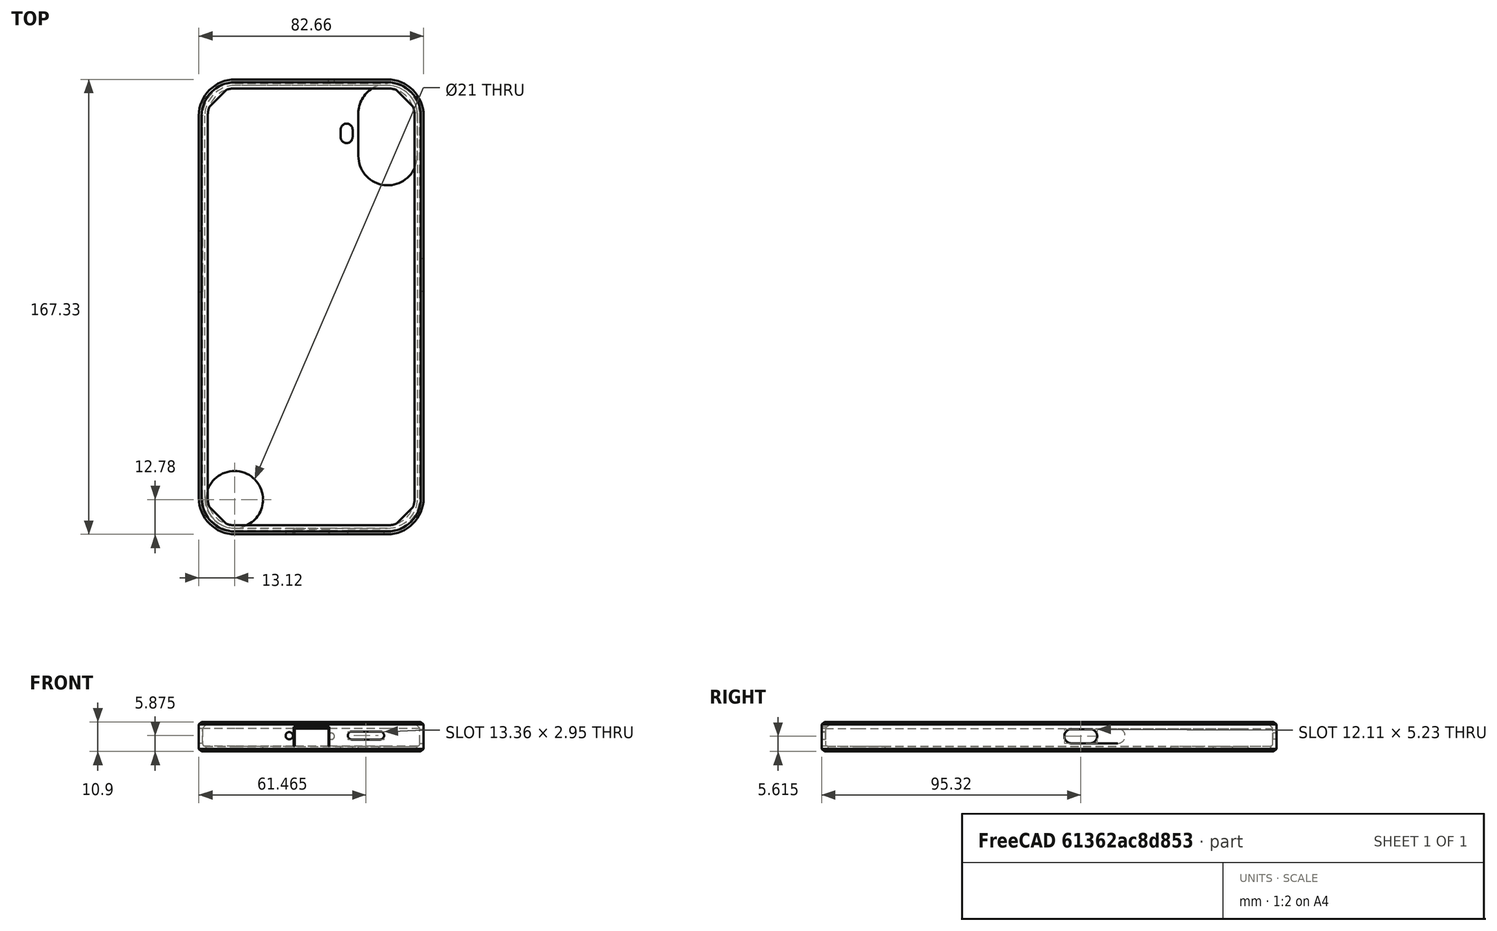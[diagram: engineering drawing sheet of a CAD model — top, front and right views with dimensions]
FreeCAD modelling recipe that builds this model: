
FCSTD DOCUMENT  (FreeCAD 0.22R38506 (Git))
Label: cmf_phone_1_v3
License: All rights reserved
LicenseURL: https://en.wikipedia.org/wiki/All_rights_reserved
objects: Sketcher::SketchObject×8, PartDesign::Pocket×4, Mesh::Feature×2, PartDesign::Pad×2, App::LinkGroup×1, PartDesign::AdditivePipe×1, PartDesign::Plane×1, PartDesign::Mirrored×1, PartDesign::Body×1, App::Part×1, Image::ImagePlane×1
note: 41 computed .brp shape members not serialized (recipe doc carries the construction recipe); baked Part::Feature solids carry a one-line shape summary decoded from their .brp

FEATURE [Mesh::Feature] cmf1_case  label="cmf1-case"
  Placement = pos=(-575.3,0,-7.05e-14) rot=(0,1,0;3.14159rad)
FEATURE [App::LinkGroup] LinkGroup
  ElementList = -> [cmf1_case]
  LinkMode = 0
  Placement = pos=(0.5,-5.96046e-08,0.4) rot=(0,0,1;0rad)
FEATURE [Sketcher::SketchObject] Sketch001  label="ProfilePathSketch"
  ArcFitTolerance = 1e-06
  AttachmentSupport = -> [XY_Plane001]
  FullyConstrained = false
  MakeInternals = false
  MapMode = 5
  sketch-geometry (5):
    g0: LineSegment StartX=0 StartY=-83.68 StartZ=0 EndX=28 EndY=-83.68 EndZ=0
    g1: ArcOfCircle CenterX=28 CenterY=-71.3528 CenterZ=0 NormalX=0 NormalY=0 NormalZ=1 AngleXU=0 Radius=12.3272 StartAngle=4.71239 EndAngle=6.28319
    g2: LineSegment StartX=40.3272 StartY=-71.3528 StartZ=0 EndX=40.3272 EndY=69.3228 EndZ=0
    g3: ArcOfCircle CenterX=28 CenterY=69.3228 CenterZ=0 NormalX=0 NormalY=0 NormalZ=1 AngleXU=0 Radius=12.3272 StartAngle=2e-16 EndAngle=1.5708
    g4: LineSegment StartX=28 StartY=81.65 StartZ=0 EndX=0 EndY=81.65 EndZ=0
  constraints (13):
    c: PointOnObject(g0,g-2)
    c: Horizontal(g0)
    c: Tangent(g1,g0) = -1.5708
    c: Vertical(g2)
    c: Tangent(g2,g1) = -1.5708
    c: DistanceX(g-1,g0) = 28
    c: DistanceY(g0,g-1) = 83.68
    c: PointOnObject(g4,g-2)
    c: Horizontal(g4)
    c: Equal(g0,g4)
    c: DistanceY(g0,g4) = 165.33
    c: Tangent(g4,g3) = -1.5708
    c: Tangent(g3,g2) = -1.5708
FEATURE [Sketcher::SketchObject] Sketch  label="ProfileSketch"
  ArcFitTolerance = 1e-06
  AttachmentSupport = -> [Sketch001]
  FullyConstrained = false
  MakeInternals = false
  MapMode = 7
  Placement = pos=(0,-83.68,0) rot=(0.57735,-0.57735,-0.57735;2.0944rad)
  sketch-geometry (11):
    g0: ArcOfCircle CenterX=-1.2 CenterY=2.8 CenterZ=0 NormalX=0 NormalY=0 NormalZ=1 AngleXU=0 Radius=0.8 StartAngle=4.71239 EndAngle=6.28319
    g1: LineSegment StartX=-0.4 StartY=2.8 StartZ=0 EndX=-0.4 EndY=8.4 EndZ=0
    g2: ArcOfCircle CenterX=-1.46903 CenterY=8.10997 CenterZ=0 NormalX=0 NormalY=0 NormalZ=1 AngleXU=0 Radius=1.10767 StartAngle=0.264929 EndAngle=0.855211
    g3: LineSegment StartX=-0.742328 StartY=8.94594 StartZ=0 EndX=-2.3 EndY=10.3 EndZ=0
    g4: LineSegment StartX=-2.3 StartY=10.3 StartZ=0 EndX=-2.3 EndY=10.9 EndZ=0
    g5: LineSegment StartX=-1.2 StartY=2 StartZ=0 EndX=-1.2 EndY=0 EndZ=0
    g6: LineSegment StartX=-1.2 StartY=0 StartZ=0 EndX=0 EndY=0 EndZ=0
    g7: LineSegment StartX=0 StartY=0 StartZ=0 EndX=1 EndY=1 EndZ=0
    g8: LineSegment StartX=1 StartY=1 StartZ=0 EndX=1 EndY=9.9 EndZ=0
    g9: LineSegment StartX=1 StartY=9.9 StartZ=0 EndX=-4e-16 EndY=10.9 EndZ=0
    g10: LineSegment StartX=-2.3 StartY=10.9 StartZ=0 EndX=-4e-16 EndY=10.9 EndZ=0
  constraints (31):
    c: Vertical(g1)
    c: Coincident(g2,g1)
    c: Angle(g3,g1) = 2.28638
    c: Coincident(g4,g3)
    c: Vertical(g4)
    c: Radius(g0) = 0.8
    c: Tangent(g1,g0) = -1.5708
    c: Coincident(g5,g0)
    c: Vertical(g5)
    c: Perpendicular(g0,g5)
    c: DistanceY(g5,g5) = 2  'bottom'
    c: Coincident(g6,g5)
    c: Horizontal(g6)
    c: DistanceX(g6,g6) = 1.2
    c: Coincident(g7,g6)
    c: Angle(g7,g6) = 2.35619
    c: DistanceY(g7,g7) = 1
    c: Coincident(g8,g7)
    c: Vertical(g8)
    c: Coincident(g8,g9)
    c: Angle(g9,g8) = 2.35619
    c: Coincident(g10,g4)
    c: Coincident(g10,g9)
    c: Horizontal(g10)
    c: Equal(g7,g9)
    c: Tangent(g3,g2) = -1.5708
    c: DistanceY(g1,g1) = 5.6
    c: Coincident(g6,g-1)
    c: Distance(g4,g4) = 0.6
    c: DistanceX(g3,g0) = 1.1
    c: DistanceY(g0,g3) = 8.3
FEATURE [PartDesign::AdditivePipe] AdditivePipe
  AuxilleryCurvelinear = true
  AuxillerySpineTangent = false
  Binormal = (0,0,0)
  Mode = 0
  Profile = -> Sketch
  Refine = true
  Spine = -> Sketch001 [Edge1,Edge2,Edge3,Edge4,Edge5]
  SpineTangent = false
  Suppressed = false
  Transformation = 0
  Transition = 0
FEATURE [PartDesign::Plane] DatumPlane  label="CaseTopDatumPlane"
  AttachmentSupport = -> [AdditivePipe]
  Length = 106.175
  MapMode = 5
  Placement = pos=(0,0,10.9) rot=(0,0,1;0rad)
  ResizeMode = 0
  Width = 190.851
FEATURE [Sketcher::SketchObject] Sketch002  label="CornerClampSketch"
  ArcFitTolerance = 1e-06
  AttachmentSupport = -> [DatumPlane]
  ExternalGeometry = -> [AdditivePipe]
  FullyConstrained = true
  MakeInternals = false
  MapMode = 5
  Placement = pos=(0,0,10.9) rot=(0,0,1;0rad)
  sketch-geometry (8):
    g0: LineSegment StartX=31.2599 StartY=-80.8353 StartZ=0 EndX=37.4825 EndY=-74.6127 EndZ=0
    g1: ArcOfCircle CenterX=28 CenterY=-71.3528 CenterZ=0 NormalX=0 NormalY=0 NormalZ=1 AngleXU=0 Radius=10.0272 StartAngle=5.04352 EndAngle=5.95206
    g2: LineSegment [constr] StartX=28 StartY=-81.38 StartZ=0 EndX=31.2599 EndY=-80.8353 EndZ=0
    g3: LineSegment [constr] StartX=38.0272 StartY=-71.3528 StartZ=0 EndX=37.4825 EndY=-74.6127 EndZ=0
    g4: LineSegment StartX=31.2599 StartY=78.8053 StartZ=0 EndX=37.4825 EndY=72.5827 EndZ=0
    g5: LineSegment [constr] StartX=28 StartY=79.35 StartZ=0 EndX=31.2599 EndY=78.8053 EndZ=0
    g6: LineSegment [constr] StartX=38.0272 StartY=69.3228 StartZ=0 EndX=37.4825 EndY=72.5827 EndZ=0
    g7: ArcOfCircle CenterX=28 CenterY=69.3228 CenterZ=0 NormalX=0 NormalY=0 NormalZ=1 AngleXU=0 Radius=10.0272 StartAngle=0.331128 EndAngle=1.23967
  constraints (21):
    c: PointOnObject(g0,g-3)
    c: Tangent(g1,g-3) = -1.5708
    c: Coincident(g0,g1)
    c: Coincident(g0,g1)
    c: Coincident(g2,g-3)
    c: Coincident(g3,g0)
    c: Coincident(g0,g2)
    c: Equal(g3,g2)
    c: Distance(g0,g0) = 8.8
    c: PointOnObject(g4,g-4)
    c: PointOnObject(g4,g-4)
    c: Coincident(g5,g-4)
    c: Coincident(g5,g4)
    c: Coincident(g6,g-4)
    c: Coincident(g6,g4)
    c: Equal(g6,g5)
    c: Coincident(g7,g4)
    c: Coincident(g7,g4)
    c: Equal(g-4,g7)
    c: Equal(g4,g0)
    c: Coincident(g3,g-3)
FEATURE [PartDesign::Pad] Pad  label="CornerClampPad"
  BaseFeature = -> AdditivePipe
  Direction = (0,0,1)
  Length = 0.6
  Length2 = 10
  Profile = -> Sketch002
  ReferenceAxis = -> Sketch002 [N_Axis]
  Refine = true
  Reversed = true
  Suppressed = false
  Type = 0
FEATURE [PartDesign::Mirrored] Mirrored  label="ProfileMirrored"
  BaseFeature = -> Pad
  MirrorPlane = -> Sketch002 [V_Axis]
  Originals = -> [Pad,AdditivePipe]
  Refine = true
  Suppressed = false
  TransformMode = 0
FEATURE [Sketcher::SketchObject] Sketch003  label="BottomSketch"
  ArcFitTolerance = 1e-06
  AttachmentSupport = -> [XY_Plane001]
  ExternalGeometry = -> [Mirrored]
  FullyConstrained = false
  MakeInternals = false
  MapMode = 5
  sketch-geometry (18):
    g0: ArcOfCircle CenterX=13.02 CenterY=64.19 CenterZ=0 NormalX=0 NormalY=0 NormalZ=1 AngleXU=0 Radius=2.2 StartAngle=2.3e-15 EndAngle=3.14159
    g1: ArcOfCircle CenterX=13.02 CenterY=61.45 CenterZ=0 NormalX=0 NormalY=0 NormalZ=1 AngleXU=0 Radius=2.2 StartAngle=3.14159 EndAngle=6.28319
    g2: LineSegment StartX=15.22 StartY=64.19 StartZ=0 EndX=15.22 EndY=61.45 EndZ=0
    g3: LineSegment StartX=10.82 StartY=64.19 StartZ=0 EndX=10.82 EndY=61.45 EndZ=0
    g4: Circle CenterX=-28.21 CenterY=-71.9 CenterZ=0 NormalX=0 NormalY=0 NormalZ=1 AngleXU=0 Radius=10.5
    g5: LineSegment StartX=-39.3007 StartY=70.6493 StartZ=0 EndX=-39.3007 EndY=-71.7132 EndZ=0
    g6: LineSegment StartX=-28.5339 StartY=-82.48 StartZ=0 EndX=28.5 EndY=-82.48 EndZ=0
    g7: LineSegment StartX=39.2668 StartY=-71.7132 StartZ=0 EndX=39.2668 EndY=70.6832 EndZ=0
    g8: LineSegment StartX=28.5 StartY=81.45 StartZ=0 EndX=-28.5 EndY=81.45 EndZ=0
    g9: ArcOfCircle CenterX=-28.5 CenterY=70.6493 CenterZ=0 NormalX=0 NormalY=0 NormalZ=1 AngleXU=0 Radius=10.8007 StartAngle=1.5708 EndAngle=3.14159
    g10: ArcOfCircle CenterX=-28.5339 CenterY=-71.7132 CenterZ=0 NormalX=0 NormalY=0 NormalZ=1 AngleXU=0 Radius=10.7668 StartAngle=3.14159 EndAngle=4.71239
    g11: ArcOfCircle CenterX=28.5 CenterY=-71.7132 CenterZ=0 NormalX=0 NormalY=0 NormalZ=1 AngleXU=0 Radius=10.7668 StartAngle=4.71239 EndAngle=6.28319
    g12: ArcOfCircle CenterX=28.5 CenterY=70.6832 CenterZ=0 NormalX=0 NormalY=0 NormalZ=1 AngleXU=0 Radius=10.7668 StartAngle=0 EndAngle=1.5708
    g13: GeomPoint [constr] X=39.2668 Y=-82.48 Z=0
    g14: ArcOfCircle CenterX=28.14 CenterY=70.19 CenterZ=0 NormalX=0 NormalY=0 NormalZ=1 AngleXU=0 Radius=10.8 StartAngle=0 EndAngle=3.14159
    g15: ArcOfCircle CenterX=28.14 CenterY=54.49 CenterZ=0 NormalX=0 NormalY=0 NormalZ=1 AngleXU=0 Radius=10.8 StartAngle=3.14159 EndAngle=6.28319
    g16: LineSegment StartX=38.94 StartY=70.19 StartZ=0 EndX=38.94 EndY=54.49 EndZ=0
    g17: LineSegment StartX=17.34 StartY=70.19 StartZ=0 EndX=17.34 EndY=54.49 EndZ=0
  constraints (39):
    c: Tangent(g0,g2) = 1.5708
    c: Tangent(g0,g3) = -1.5708
    c: Tangent(g1,g2) = 1.5708
    c: Tangent(g1,g3) = -1.5708
    c: Equal(g0,g1)
    c: Vertical(g3)
    c: DistanceX(g0,g0) = 4.4
    c: DistanceY(g3,g3) = 2.74
    c: Diameter(g4) = 21
    c: DistanceY(g4,g-1) = 71.9
    c: DistanceX(g4,g-1) = 28.21
    c: Tangent(g5,g9) = -1.5708
    c: Tangent(g5,g10) = -1.5708
    c: Tangent(g6,g10) = -1.5708
    c: Tangent(g6,g11) = -1.5708
    c: Tangent(g7,g11) = -1.5708
    c: Tangent(g7,g12) = -1.5708
    c: Tangent(g8,g12) = -1.5708
    c: Tangent(g8,g9) = -1.5708
    c: Vertical(g5)
    c: Vertical(g7)
    c: Horizontal(g6)
    c: Horizontal(g8)
    c: Equal(g10,g11)
    c: Equal(g11,g12)
    c: PointOnObject(g13,g6)
    c: PointOnObject(g13,g7)
    c: DistanceY(g-1,g1) = 61.45
    c: DistanceX(g-1,g1) = 13.02
    c: Tangent(g14,g16) = 1.5708
    c: Tangent(g14,g17) = -1.5708
    c: Tangent(g15,g16) = 1.5708
    c: Tangent(g15,g17) = -1.5708
    c: Equal(g14,g15)
    c: Vertical(g16)
    c: DistanceX(g15,g15) = 21.6
    c: DistanceY(g0,g14) = 6
    c: DistanceX(g0,g14) = 4.32
    c: DistanceY(g16,g16) = 15.7
FEATURE [PartDesign::Pad] Pad001  label="BottomPad"
  BaseFeature = -> Mirrored
  Direction = (0,0,1)
  Length = 1.8
  Length2 = 10
  Profile = -> Sketch003
  ReferenceAxis = -> Sketch003 [N_Axis]
  Refine = true
  Suppressed = false
  Type = 0
  expr: Length = <<ProfileSketch>>.Constraints.bottom - 0.2 mm
FEATURE [Sketcher::SketchObject] Sketch004  label="LeftHoleSketch"
  ArcFitTolerance = 1e-06
  AttachmentSupport = -> [YZ_Plane001]
  FullyConstrained = true
  MakeInternals = false
  MapMode = 5
  Placement = pos=(0,0,0) rot=(0.57735,0.57735,0.57735;2.0944rad)
  expr: Constraints[8] = <<ProfileSketch>>.Constraints.bottom + 1 mm
  sketch-geometry (4):
    g0: ArcOfCircle CenterX=7.18 CenterY=5.7 CenterZ=0 NormalX=0 NormalY=0 NormalZ=1 AngleXU=0 Radius=2.7 StartAngle=1.5708 EndAngle=4.71239
    g1: ArcOfCircle CenterX=24.25 CenterY=5.7 CenterZ=0 NormalX=0 NormalY=0 NormalZ=1 AngleXU=0 Radius=2.7 StartAngle=4.71239 EndAngle=7.85398
    g2: LineSegment StartX=7.18 StartY=8.4 StartZ=0 EndX=24.25 EndY=8.4 EndZ=0
    g3: LineSegment StartX=7.18 StartY=3 StartZ=0 EndX=24.25 EndY=3 EndZ=0
  constraints (10):
    c: Tangent(g0,g2) = 1.5708
    c: Tangent(g0,g3) = -1.5708
    c: Tangent(g1,g2) = 1.5708
    c: Tangent(g1,g3) = -1.5708
    c: Equal(g0,g1)
    c: Horizontal(g2)
    c: DistanceY(g0,g0) = 5.4
    c: DistanceX(g-1,g0) = 7.18
    c: Distance(g0,g-1) = 3
    c: DistanceX(g2,g2) = 17.07
FEATURE [PartDesign::Pocket] Pocket  label="LeftPocket"
  BaseFeature = -> Pad001
  Direction = (-1,0,0)
  Length = 5
  Length2 = 5
  Profile = -> Sketch004
  ReferenceAxis = -> Sketch004 [N_Axis]
  Refine = true
  Suppressed = false
  Type = 1
FEATURE [Sketcher::SketchObject] Sketch005  label="RightPocketSketch"
  ArcFitTolerance = 1e-06
  AttachmentSupport = -> [YZ_Plane001]
  FullyConstrained = true
  MakeInternals = false
  MapMode = 5
  Placement = pos=(0,0,0) rot=(0.57735,-0.57735,-0.57735;2.0944rad)
  expr: Constraints[7] = <<ProfileSketch>>.Constraints.bottom + 1 mm
  sketch-geometry (4):
    g0: ArcOfCircle CenterX=-14.08 CenterY=5.615 CenterZ=0 NormalX=0 NormalY=0 NormalZ=1 AngleXU=0 Radius=2.615 StartAngle=1.5708 EndAngle=4.71239
    g1: ArcOfCircle CenterX=-7.2 CenterY=5.615 CenterZ=0 NormalX=0 NormalY=0 NormalZ=1 AngleXU=0 Radius=2.615 StartAngle=4.71239 EndAngle=7.85398
    g2: LineSegment StartX=-14.08 StartY=8.23 StartZ=0 EndX=-7.2 EndY=8.23 EndZ=0
    g3: LineSegment StartX=-14.08 StartY=3 StartZ=0 EndX=-7.2 EndY=3 EndZ=0
  constraints (10):
    c: Tangent(g0,g2) = 1.5708
    c: Tangent(g0,g3) = -1.5708
    c: Tangent(g1,g2) = 1.5708
    c: Tangent(g1,g3) = -1.5708
    c: Equal(g0,g1)
    c: Horizontal(g2)
    c: DistanceY(g1,g1) = 5.23
    c: DistanceY(g-1,g1) = 3
    c: DistanceX(g1,g-1) = 7.2
    c: DistanceX(g3,g3) = 6.88
FEATURE [PartDesign::Pocket] Pocket001  label="RightPocket"
  BaseFeature = -> Pocket
  Direction = (1,0,0)
  Length = 5
  Length2 = 5
  Profile = -> Sketch005
  ReferenceAxis = -> Sketch005 [N_Axis]
  Refine = true
  Suppressed = false
  Type = 1
FEATURE [Sketcher::SketchObject] Sketch006  label="BottomPocketSketch"
  ArcFitTolerance = 1e-06
  AttachmentSupport = -> [XZ_Plane001]
  FullyConstrained = true
  MakeInternals = false
  MapMode = 5
  Placement = pos=(0,0,0) rot=(0,0.707107,0.707107;3.14159rad)
  expr: Constraints[27] = <<ProfileSketch>>.Constraints.bottom
  expr: Constraints[35] = <<ProfileSketch>>.Constraints.bottom + 3.8 mm
  expr: Constraints[9] = <<ProfileSketch>>.Constraints.bottom + 2.4 mm
  sketch-geometry (13):
    g0: ArcOfCircle CenterX=-25.34 CenterY=5.875 CenterZ=0 NormalX=0 NormalY=0 NormalZ=1 AngleXU=0 Radius=1.475 StartAngle=1.5708 EndAngle=4.71239
    g1: ArcOfCircle CenterX=-14.93 CenterY=5.875 CenterZ=0 NormalX=0 NormalY=0 NormalZ=1 AngleXU=0 Radius=1.475 StartAngle=4.71239 EndAngle=7.85398
    g2: LineSegment StartX=-25.34 StartY=7.35 StartZ=0 EndX=-14.93 EndY=7.35 EndZ=0
    g3: LineSegment StartX=-25.34 StartY=4.4 StartZ=0 EndX=-14.93 EndY=4.4 EndZ=0
    g4: LineSegment StartX=-6.69 StartY=2 StartZ=0 EndX=-6.69 EndY=9.02 EndZ=0
    g5: LineSegment StartX=-6.69 StartY=9.02 StartZ=0 EndX=6.41 EndY=9.02 EndZ=0
    g6: LineSegment StartX=6.41 StartY=9.02 StartZ=0 EndX=6.41 EndY=2 EndZ=0
    g7: LineSegment StartX=6.41 StartY=2 StartZ=0 EndX=6.11 EndY=2 EndZ=0
    g8: LineSegment StartX=6.11 StartY=2 StartZ=0 EndX=6.11 EndY=8.42 EndZ=0
    g9: LineSegment StartX=6.11 StartY=8.42 StartZ=0 EndX=-6.39 EndY=8.42 EndZ=0
    g10: LineSegment StartX=-6.39 StartY=8.42 StartZ=0 EndX=-6.39 EndY=2 EndZ=0
    g11: LineSegment StartX=-6.39 StartY=2 StartZ=0 EndX=-6.69 EndY=2 EndZ=0
    g12: Circle CenterX=8.08 CenterY=5.8 CenterZ=0 NormalX=0 NormalY=0 NormalZ=1 AngleXU=0 Radius=1.345
  constraints (37):
    c: Tangent(g0,g2) = 1.5708
    c: Tangent(g0,g3) = -1.5708
    c: Tangent(g1,g2) = 1.5708
    c: Tangent(g1,g3) = -1.5708
    c: Equal(g0,g1)
    c: Horizontal(g2)
    c: DistanceY(g0,g0) = 2.95
    c: DistanceX(g3,g3) = 10.41
    c: DistanceX(g1,g-1) = 14.93
    c: DistanceY(g-1,g1) = 4.4
    c: Vertical(g4)
    c: Coincident(g4,g5)
    c: Horizontal(g5)
    c: Coincident(g5,g6)
    c: Vertical(g6)
    c: Coincident(g6,g7)
    c: Coincident(g7,g8)
    c: Vertical(g8)
    c: Coincident(g8,g9)
    c: Coincident(g9,g10)
    c: Vertical(g10)
    c: Coincident(g10,g11)
    c: Coincident(g11,g4)
    c: Horizontal(g11)
    c: Horizontal(g7)
    c: Equal(g11,g7)
    c: DistanceY(g9,g4) = 0.6
    c: DistanceY(g-1,g10) = 2
    c: Horizontal(g7,g10)
    c: DistanceY(g10,g10) = 6.42
    c: DistanceX(g9,g9) = 12.5
    c: DistanceX(g4,g9) = 0.3
    c: DistanceX(g10,g-1) = 6.39
    c: Horizontal(g9)
    c: DistanceX(g-1,g12) = 8.08
    c: DistanceY(g-1,g12) = 5.8
    c: Diameter(g12) = 2.69
FEATURE [PartDesign::Pocket] Pocket002  label="BottomPocket"
  BaseFeature = -> Pocket001
  Direction = (0,-1,2e-16)
  Length = 5
  Length2 = 5
  Profile = -> Sketch006
  ReferenceAxis = -> Sketch006 [N_Axis]
  Refine = true
  Suppressed = false
  Type = 1
FEATURE [Sketcher::SketchObject] Sketch007  label="TopPocketSketch"
  ArcFitTolerance = 1e-06
  AttachmentSupport = -> [XZ_Plane001]
  ExternalGeometry = -> [Pocket002]
  FullyConstrained = true
  MakeInternals = false
  MapMode = 5
  Placement = pos=(0,0,0) rot=(1,0,0;1.5708rad)
  sketch-geometry (3):
    g0: Circle CenterX=7.4 CenterY=5.6 CenterZ=0 NormalX=0 NormalY=0 NormalZ=1 AngleXU=0 Radius=1.15
    g1: LineSegment [constr] StartX=7.4 StartY=5.6 StartZ=0 EndX=39.9272 EndY=8.4 EndZ=0
    g2: LineSegment [constr] StartX=7.4 StartY=5.6 StartZ=0 EndX=39.9272 EndY=2.8 EndZ=0
  constraints (7):
    c: Coincident(g1,g0)
    c: Coincident(g2,g0)
    c: Equal(g1,g2)
    c: Diameter(g0) = 2.3
    c: Coincident(g1,g-3)
    c: Coincident(g2,g-3)
    c: DistanceX(g-1,g0) = 7.4
FEATURE [PartDesign::Pocket] Pocket003  label="TopPocket"
  BaseFeature = -> Pocket002
  Direction = (0,1,-2e-16)
  Length = 5
  Length2 = 5
  Profile = -> Sketch007
  ReferenceAxis = -> Sketch007 [N_Axis]
  Refine = true
  Suppressed = false
  Type = 1
FEATURE [PartDesign::Body] Body
  AllowCompound = false
  Group = -> [Sketch,Sketch001,AdditivePipe,DatumPlane,Sketch002,Pad,Mirrored,Sketch003,Pad001,Sketch004,Pocket,Sketch005,Pocket001,Sketch006,Pocket002,Sketch007,Pocket003]
  Origin = -> Origin001
  Tip = -> Pocket003
FEATURE [App::Part] Part
  Group = -> [Body]
  Origin = -> Origin
FEATURE [Image::ImagePlane] screenshot_2024_07_09_alle_202352  label="screenshot-2024-07-09-alle-202352"
  Placement = pos=(0,0,0) rot=(0,-1,0;3.14159rad)
  XSize = 436.864
  YSize = 245.508
FEATURE [Mesh::Feature] Mesh  label="Body (Meshed)"
